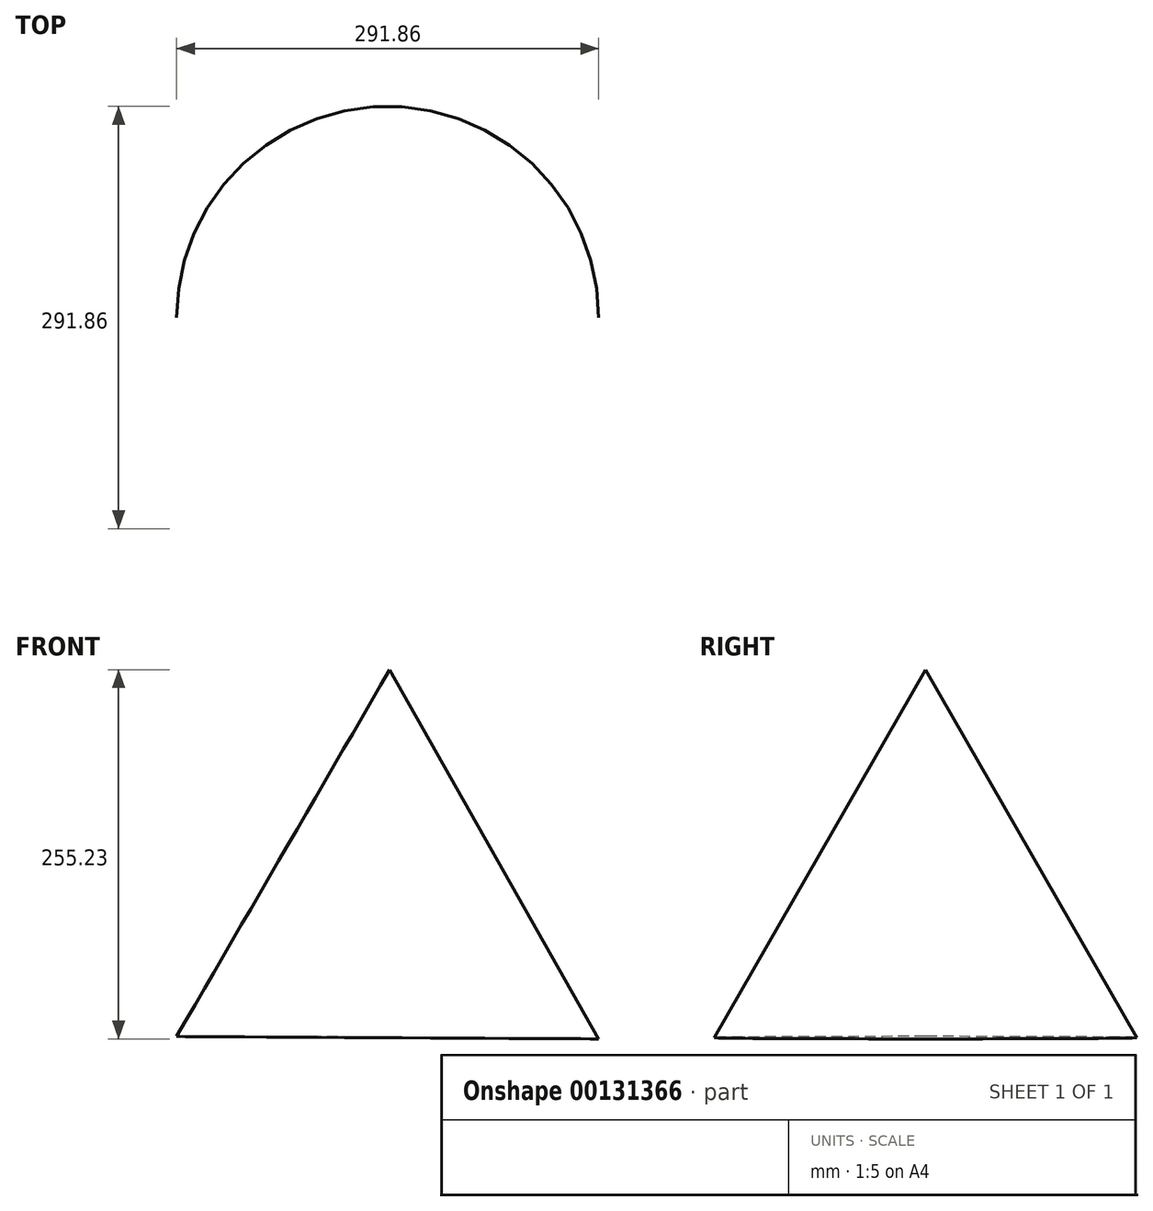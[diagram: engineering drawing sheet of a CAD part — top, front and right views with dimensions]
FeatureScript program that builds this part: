
annotation { "Feature Type Name" : "Feature", "Feature Type Description" : "" }
export const myFeature = defineFeature(function(context is Context, id is Id, definition is map)
    precondition{}
    {
        {
            var Q0;
            Q0=qCreatedBy(makeId("Front.planeOp"),FACE);
            var sketch = newSketch(context, id + "F0", { "sketchPlane" : qUnion([Q0])});
            skCircle(sketch, "E0.cCircle", {"center": v(0, 0) * mm, "radius": 84.67 * mm, "construction": true});
            skLineSegment(sketch, "E0.0", {"start": v(1.43, 169.33) * mm, "end": v(145.93, -85.9) * mm});
            skLineSegment(sketch, "E0.1", {"start": v(145.93, -85.9) * mm, "end": v(-147.35, -83.43) * mm});
            skLineSegment(sketch, "E0.2", {"start": v(-147.35, -83.43) * mm, "end": v(1.43, 169.33) * mm});
            skPoint(sketch, "E0.0.midPoint", {"position": v(73.68, 41.71) * mm});
            skLineSegment(sketch, "E1", {"start": v(1.43, 169.33) * mm, "end": v(0, -84.67) * mm});
            skSolve(sketch);
        }
        {
            var Q0;
            {var subQ0=sQuery(id+"F0.wireOp",EDGE,"E0.0");Q0=makeQuery(id+"F0.imprint","IMPRINT",FACE,{"disambiguationData":[TD([[makeQuery(id+"F0.imprint","IMPRINT",EDGE,{"derivedFrom":subQ0}),-1.0]])]});}
            var Q1;
            Q1=sQuery(id+"F0.wireOp",EDGE,"E1");
            revolve(context, id + "F1", {"entities" : qUnion([Q0]), "axis" : qUnion([Q1]), "revolveType" : RevolveType.FULL});
        }
    });
